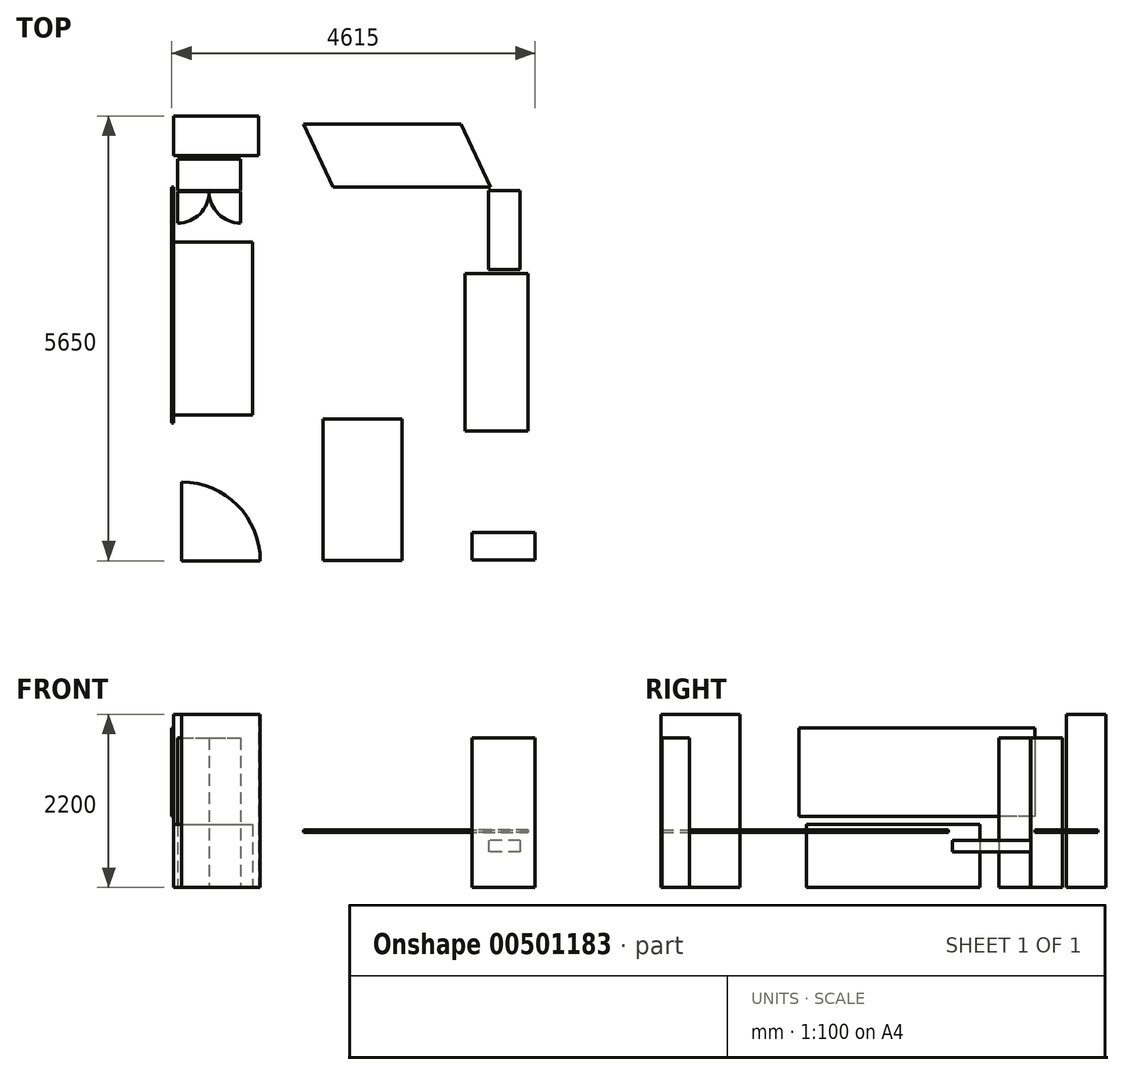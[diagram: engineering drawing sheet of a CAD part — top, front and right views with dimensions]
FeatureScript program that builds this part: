
annotation { "Feature Type Name" : "Feature", "Feature Type Description" : "" }
export const myFeature = defineFeature(function(context is Context, id is Id, definition is map)
    precondition{}
    {
        {
            var Q0;
            Q0=qCreatedBy(makeId("Top.planeOp"),FACE);
            var sketch = newSketch(context, id + "F0", { "sketchPlane" : qUnion([Q0])});
            skLineSegment(sketch, "E0.bottom", {"start": v(0, 0) * mm, "end": v(4600, 0) * mm});
            skLineSegment(sketch, "E0.top", {"start": v(0, 5650) * mm, "end": v(4600, 5650) * mm});
            skLineSegment(sketch, "E0.left", {"start": v(0, 0) * mm, "end": v(0, 5650) * mm});
            skLineSegment(sketch, "E0.right", {"start": v(4600, 0) * mm, "end": v(4600, 5650) * mm});
            skSolve(sketch);
        }
        {
            var Q0;
            Q0=qCreatedBy(makeId("Top.planeOp"),FACE);
            var sketch = newSketch(context, id + "F1", { "sketchPlane" : qUnion([Q0])});
            skLineSegment(sketch, "E1.bottom", {"start": v(0, 5650) * mm, "end": v(1080, 5650) * mm});
            skLineSegment(sketch, "E1.top", {"start": v(0, 5150) * mm, "end": v(1080, 5150) * mm});
            skLineSegment(sketch, "E1.left", {"start": v(0, 5650) * mm, "end": v(0, 5150) * mm});
            skLineSegment(sketch, "E1.right", {"start": v(1080, 5650) * mm, "end": v(1080, 5150) * mm});
            skSolve(sketch);
        }
        {
            var Q0;
            Q0=qCreatedBy(makeId("Top.planeOp"),FACE);
            var sketch = newSketch(context, id + "F2", { "sketchPlane" : qUnion([Q0])});
            skLineSegment(sketch, "E2.bottom", {"start": v(1900, 1) * mm, "end": v(2900, 1) * mm});
            skLineSegment(sketch, "E2.top", {"start": v(1900, 1201) * mm, "end": v(2900, 1201) * mm});
            skLineSegment(sketch, "E2.left", {"start": v(1900, 1) * mm, "end": v(1900, 1201) * mm});
            skLineSegment(sketch, "E2.right", {"start": v(2900, 1) * mm, "end": v(2900, 1201) * mm});
            skLineSegment(sketch, "E3.bottom", {"start": v(1900, 1801) * mm, "end": v(2900, 1801) * mm});
            skLineSegment(sketch, "E3.left", {"start": v(1900, 1801) * mm, "end": v(1900, 1201) * mm});
            skLineSegment(sketch, "E3.right", {"start": v(2900, 1801) * mm, "end": v(2900, 1201) * mm});
            skSolve(sketch);
        }
        {
            var Q0;
            Q0=qCreatedBy(makeId("Top.planeOp"),FACE);
            var sketch = newSketch(context, id + "F3", { "sketchPlane" : qUnion([Q0])});
            skArc(sketch, "E4", {"start": v(1100, 0) * mm, "mid": v(807.1, 707.1) * mm, "end": v(100, 1000) * mm});
            skLineSegment(sketch, "E5", {"start": v(1100, 0) * mm, "end": v(100, 0) * mm});
            skLineSegment(sketch, "E6", {"start": v(100, 0) * mm, "end": v(100, 1000) * mm});
            skSolve(sketch);
        }
        {
            var Q0;
            Q0=qCreatedBy(makeId("Top.planeOp"),FACE);
            var sketch = newSketch(context, id + "F4", { "sketchPlane" : qUnion([Q0])});
            skLineSegment(sketch, "E7", {"start": v(3700, 1650) * mm, "end": v(3700, 3650) * mm});
            skLineSegment(sketch, "E8", {"start": v(4500, 3650) * mm, "end": v(4500, 1650) * mm});
            skLineSegment(sketch, "E9", {"start": v(3700, 3650) * mm, "end": v(4500, 3650) * mm});
            skLineSegment(sketch, "E10", {"start": v(4500, 1650) * mm, "end": v(3700, 1650) * mm});
            skLineSegment(sketch, "E11.bottom", {"start": v(4400, 4700) * mm, "end": v(4000, 4700) * mm});
            skLineSegment(sketch, "E11.top", {"start": v(4400, 3700) * mm, "end": v(4000, 3700) * mm});
            skLineSegment(sketch, "E11.left", {"start": v(4400, 4700) * mm, "end": v(4400, 3700) * mm});
            skLineSegment(sketch, "E11.right", {"start": v(4000, 4700) * mm, "end": v(4000, 3700) * mm});
            skLineSegment(sketch, "E12", {"start": v(1650, 5550) * mm, "end": v(2023.05, 4750) * mm});
            skLineSegment(sketch, "E13", {"start": v(2023.05, 4750) * mm, "end": v(4023.05, 4750) * mm});
            skLineSegment(sketch, "E14", {"start": v(4023.05, 4750) * mm, "end": v(3650, 5550) * mm});
            skLineSegment(sketch, "E15", {"start": v(3650, 5550) * mm, "end": v(1650, 5550) * mm});
            skSolve(sketch);
        }
        {
            var Q0;
            Q0=makeQuery(id+"F3.imprint","IMPRINT",FACE,{"disambiguationData":[TD([[makeQuery(id+"F3.imprint","IMPRINT",EDGE,{"derivedFrom":sQuery(id+"F3.wireOp",EDGE,"E4")}),1.0]])]});
            extrude(context, id + "F5", {"entities" : qUnion([Q0]), "depth" : 2200 * mm});
        }
        {
            var Q0;
            Q0=makeQuery(id+"F1.imprint","IMPRINT",FACE,{"disambiguationData":[TD([[makeQuery(id+"F1.imprint","IMPRINT",EDGE,{"derivedFrom":sQuery(id+"F1.wireOp",EDGE,"E1.bottom")}),-1.0]])]});
            extrude(context, id + "F6", {"entities" : qUnion([Q0]), "depth" : 2200 * mm});
        }
        {
            var Q0;
            Q0=makeQuery(id+"F4.imprint","IMPRINT",FACE,{"disambiguationData":[TD([[makeQuery(id+"F4.imprint","IMPRINT",EDGE,{"derivedFrom":sQuery(id+"F4.wireOp",EDGE,"40FTsiH9-VMCV-BxrB-4hHm-w0bPiwGz4CeU")}),-1.0]])]});
            var Q1;
            Q1=makeQuery(id+"F4.imprint","IMPRINT",FACE,{"disambiguationData":[TD([[makeQuery(id+"F4.imprint","IMPRINT",EDGE,{"derivedFrom":sQuery(id+"F4.wireOp",EDGE,"E7")}),-1.0]])]});
            extrude(context, id + "F7", {"entities" : qUnion([Q0, Q1]), "depth" : 730 * mm, "hasSecondDirection" : true, "secondDirectionOppositeDirection" : false, "secondDirectionDepth" : 700 * mm, "offsetDistance" : 25 * mm});
        }
        {
            var Q0;
            Q0=makeQuery(id+"F4.imprint","IMPRINT",FACE,{"disambiguationData":[TD([[makeQuery(id+"F4.imprint","IMPRINT",EDGE,{"derivedFrom":sQuery(id+"F4.wireOp",EDGE,"E11.bottom")}),1.0]])]});
            extrude(context, id + "F8", {"entities" : qUnion([Q0]), "depth" : 600 * mm, "hasSecondDirection" : true, "secondDirectionOppositeDirection" : false, "secondDirectionDepth" : 450 * mm});
        }
        {
            var Q0;
            Q0=makeQuery(id+"F2.imprint","IMPRINT",FACE,{"disambiguationData":[TD([[makeQuery(id+"F2.imprint","IMPRINT",EDGE,{"derivedFrom":sQuery(id+"F2.wireOp",EDGE,"E2.bottom")}),1.0]])]});
            var Q1;
            Q1=makeQuery(id+"F2.imprint","IMPRINT",FACE,{"disambiguationData":[TD([[makeQuery(id+"F2.imprint","IMPRINT",EDGE,{"derivedFrom":sQuery(id+"F2.wireOp",EDGE,"E3.bottom")}),-1.0]])]});
            extrude(context, id + "F9", {"entities" : qUnion([Q0, Q1]), "depth" : 730 * mm, "hasSecondDirection" : true, "secondDirectionOppositeDirection" : false, "secondDirectionDepth" : 700 * mm});
        }
        {
            var Q0;
            Q0=qCreatedBy(makeId("Top.planeOp"),FACE);
            var sketch = newSketch(context, id + "F10", { "sketchPlane" : qUnion([Q0])});
            skLineSegment(sketch, "E16.bottom", {"start": v(0, 4050) * mm, "end": v(1000, 4050) * mm});
            skLineSegment(sketch, "E16.top", {"start": v(0, 1850) * mm, "end": v(1000, 1850) * mm});
            skLineSegment(sketch, "E16.left", {"start": v(0, 4050) * mm, "end": v(0, 1850) * mm});
            skLineSegment(sketch, "E16.right", {"start": v(1000, 4050) * mm, "end": v(1000, 1850) * mm});
            skPoint(sketch, "E17.firstSnap0", {"position": v(0, 2950) * mm});
            skSolve(sketch);
        }
        {
            var Q0;
            Q0=makeQuery(id+"F4.imprint","IMPRINT",FACE,{"disambiguationData":[TD([[makeQuery(id+"F4.imprint","IMPRINT",EDGE,{"derivedFrom":sQuery(id+"F4.wireOp",EDGE,"E12")}),1.0]])]});
            extrude(context, id + "F11", {"entities" : qUnion([Q0]), "depth" : 730 * mm, "offsetDistance" : 25 * mm, "hasSecondDirection" : true, "secondDirectionOppositeDirection" : false, "secondDirectionDepth" : 700 * mm});
        }
        {
            var Q0;
            Q0=qCreatedBy(makeId("Right.planeOp"),FACE);
            var sketch = newSketch(context, id + "F12", { "sketchPlane" : qUnion([Q0])});
            skLineSegment(sketch, "E18.bottom", {"start": v(4750, 2030) * mm, "end": v(1750, 2030) * mm});
            skLineSegment(sketch, "E18.top", {"start": v(4750, 900) * mm, "end": v(1750, 900) * mm});
            skLineSegment(sketch, "E18.left", {"start": v(4750, 2030) * mm, "end": v(4750, 900) * mm});
            skLineSegment(sketch, "E18.right", {"start": v(1750, 2030) * mm, "end": v(1750, 900) * mm});
            skSolve(sketch);
        }
        {
            var Q0;
            Q0=makeQuery(id+"F12.imprint","IMPRINT",FACE,{"disambiguationData":[TD([[makeQuery(id+"F12.imprint","IMPRINT",EDGE,{"derivedFrom":sQuery(id+"F12.wireOp",EDGE,"E18.bottom")}),1.0]])]});
            extrude(context, id + "F13", {"entities" : qUnion([Q0]), "oppositeDirection" : true, "depth" : 25 * mm, "offsetDistance" : 25 * mm});
        }
        {
            var Q0;
            Q0 = qSketchRegion(id + "F10", true);
            extrude(context, id + "F14", {"entities" : qUnion([Q0]), "depth" : 800 * mm, "offsetDistance" : 25 * mm});
        }
        {
            var Q0;
            Q0=qCreatedBy(makeId("Top.planeOp"),FACE);
            var sketch = newSketch(context, id + "F15", { "sketchPlane" : qUnion([Q0])});
            skLineSegment(sketch, "E19.bottom", {"start": v(50, 5100) * mm, "end": v(850, 5100) * mm});
            skLineSegment(sketch, "E19.top", {"start": v(50, 4700) * mm, "end": v(850, 4700) * mm});
            skLineSegment(sketch, "E19.left", {"start": v(50, 5100) * mm, "end": v(50, 4700) * mm});
            skLineSegment(sketch, "E19.right", {"start": v(850, 5100) * mm, "end": v(850, 4700) * mm});
            skLineSegment(sketch, "E20.bottom", {"start": v(4590, 10) * mm, "end": v(3790, 10) * mm});
            skLineSegment(sketch, "E20.top", {"start": v(4590, 360) * mm, "end": v(3790, 360) * mm});
            skLineSegment(sketch, "E20.left", {"start": v(4590, 10) * mm, "end": v(4590, 360) * mm});
            skLineSegment(sketch, "E20.right", {"start": v(3790, 10) * mm, "end": v(3790, 360) * mm});
            skSolve(sketch);
        }
        {
            var Q0;
            Q0=makeQuery(id+"F15.imprint","IMPRINT",FACE,{"disambiguationData":[TD([[makeQuery(id+"F15.imprint","IMPRINT",EDGE,{"derivedFrom":sQuery(id+"F15.wireOp",EDGE,"E19.bottom")}),-1.0]])]});
            var Q1;
            Q1=makeQuery(id+"F15.imprint","IMPRINT",FACE,{"disambiguationData":[TD([[makeQuery(id+"F15.imprint","IMPRINT",EDGE,{"derivedFrom":sQuery(id+"F15.wireOp",EDGE,"E20.bottom")}),-1.0]])]});
            extrude(context, id + "F16", {"entities" : qUnion([Q0, Q1]), "operationType" : NewBodyOperationType.ADD, "depth" : 1900 * mm, "offsetDistance" : 25 * mm});
        }
        {
            var Q0;
            Q0=qCreatedBy(makeId("Top.planeOp"),FACE);
            var sketch = newSketch(context, id + "F17", { "sketchPlane" : qUnion([Q0])});
            skLineSegment(sketch, "E21", {"start": v(50, 4690) * mm, "end": v(850, 4690) * mm});
            skArc(sketch, "E22", {"start": v(50, 4290) * mm, "mid": v(332.84, 4407.16) * mm, "end": v(450, 4690) * mm});
            skArc(sketch, "E23", {"start": v(450, 4690) * mm, "mid": v(567.16, 4407.16) * mm, "end": v(850, 4290) * mm});
            skLineSegment(sketch, "E24", {"start": v(50, 4690) * mm, "end": v(50, 4290) * mm});
            skLineSegment(sketch, "E25", {"start": v(850, 4690) * mm, "end": v(850, 4290) * mm});
            skSolve(sketch);
        }
        {
            var Q0;
            Q0 = qSketchRegion(id + "F17", true);
            extrude(context, id + "F18", {"entities" : qUnion([Q0]), "operationType" : NewBodyOperationType.ADD, "depth" : 1900 * mm, "offsetDistance" : 25 * mm});
        }
    });
